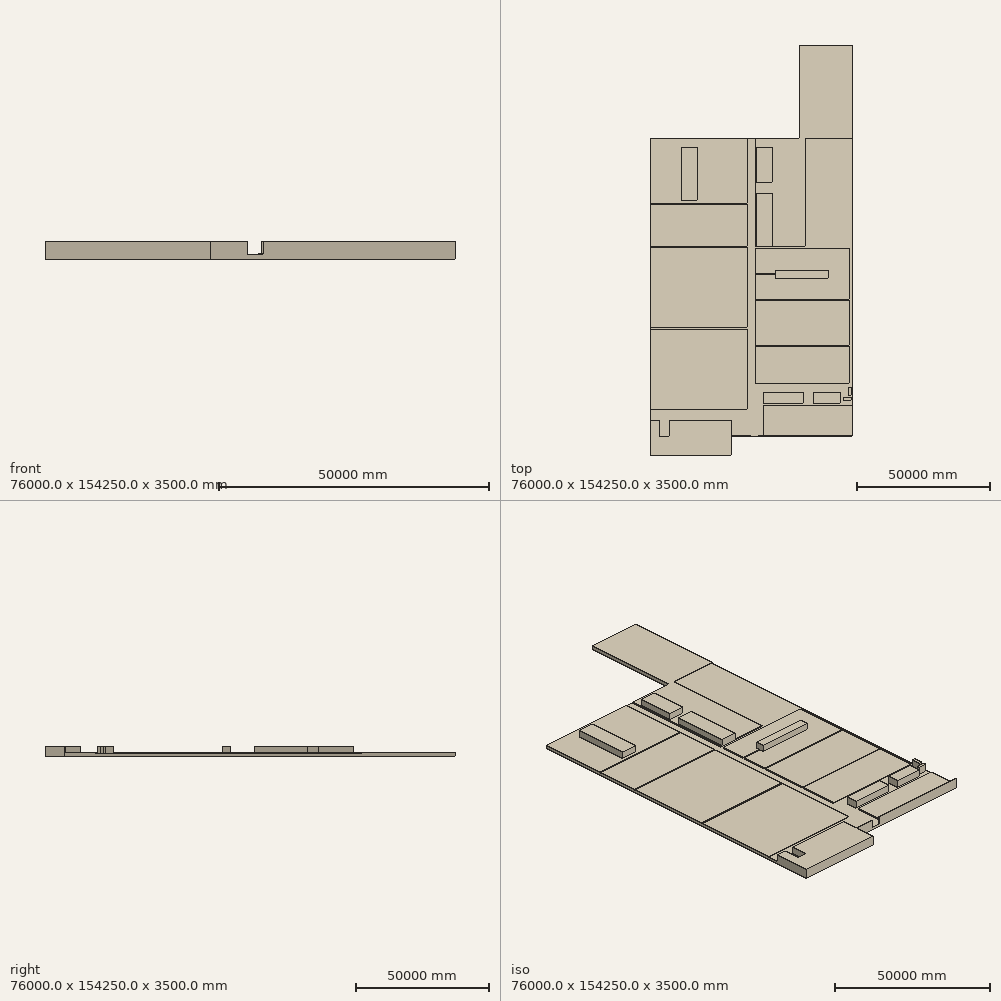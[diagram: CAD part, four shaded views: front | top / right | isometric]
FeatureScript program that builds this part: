
annotation { "Feature Type Name" : "Feature", "Feature Type Description" : "" }
export const myFeature = defineFeature(function(context is Context, id is Id, definition is map)
    precondition{}
    {
        {
            var Q0;
            Q0=qCreatedBy(makeId("Top.planeOp"),FACE);
            var sketch = newSketch(context, id + "F0", { "sketchPlane" : qUnion([Q0])});
            skLineSegment(sketch, "E0.top", {"start": v(0, 112000) * mm, "end": v(56000, 112000) * mm});
            skLineSegment(sketch, "E0.left", {"start": v(0, 0) * mm, "end": v(0, 112000) * mm});
            skLineSegment(sketch, "E0.right", {"start": v(76000, 0) * mm, "end": v(76000, 112000) * mm});
            skLineSegment(sketch, "E1", {"start": v(76000, 112000) * mm, "end": v(76000, 147000) * mm});
            skLineSegment(sketch, "E2", {"start": v(76000, 147000) * mm, "end": v(56000, 147000) * mm});
            skLineSegment(sketch, "E3", {"start": v(56000, 147000) * mm, "end": v(56000, 112000) * mm});
            skLineSegment(sketch, "E4", {"start": v(0, 0) * mm, "end": v(0, -7250) * mm});
            skLineSegment(sketch, "E5", {"start": v(0, -7250) * mm, "end": v(30500, -7250) * mm});
            skLineSegment(sketch, "E6", {"start": v(30500, -7250) * mm, "end": v(30500, -250) * mm});
            skLineSegment(sketch, "E7", {"start": v(30500, 0) * mm, "end": v(76000, 0) * mm});
            skLineSegment(sketch, "E8", {"start": v(30500, -250) * mm, "end": v(30500, -7250) * mm});
            skLineSegment(sketch, "E9", {"start": v(30500, 0) * mm, "end": v(30500, -250) * mm});
            skSolve(sketch);
        }
        {
            var Q0;
            Q0=qSketchRegion(id+"F0",true);
            extrude(context, id + "F1", {"entities" : qUnion([Q0]), "oppositeDirection" : true, "depth" : 1000 * mm});
        }
        {
            var Q0;
            Q0=makeQuery(id+"F0.imprint","IMPRINT",FACE,{"disambiguationData":[TD([[makeQuery(id+"F0.imprint","IMPRINT",EDGE,{"derivedFrom":sQuery(id+"F0.wireOp",EDGE,"E0.top")}),-1.0]])]});
            var sketch = newSketch(context, id + "F2", { "sketchPlane" : qUnion([Q0])});
            skLineSegment(sketch, "E10.bottom", {"start": v(0, 112000) * mm, "end": v(36500, 112000) * mm});
            skLineSegment(sketch, "E10.top", {"start": v(0, 87500) * mm, "end": v(36500, 87500) * mm});
            skLineSegment(sketch, "E10.left", {"start": v(0, 112000) * mm, "end": v(0, 87500) * mm});
            skLineSegment(sketch, "E10.right", {"start": v(36500, 112000) * mm, "end": v(36500, 87500) * mm});
            skLineSegment(sketch, "E11.bottom", {"start": v(0, 87000) * mm, "end": v(36500, 87000) * mm});
            skLineSegment(sketch, "E11.top", {"start": v(0, 71500) * mm, "end": v(36500, 71500) * mm});
            skLineSegment(sketch, "E11.left", {"start": v(0, 87000) * mm, "end": v(0, 71500) * mm});
            skLineSegment(sketch, "E11.right", {"start": v(36500, 87000) * mm, "end": v(36500, 71500) * mm});
            skLineSegment(sketch, "E12.bottom", {"start": v(0, 71000) * mm, "end": v(36500, 71000) * mm});
            skLineSegment(sketch, "E12.left", {"start": v(0, 71000) * mm, "end": v(0, 40750) * mm});
            skLineSegment(sketch, "E12.right", {"start": v(36500, 71000) * mm, "end": v(36500, 40750) * mm});
            skLineSegment(sketch, "E13.bottom", {"start": v(39500, 71500) * mm, "end": v(58500, 71500) * mm});
            skLineSegment(sketch, "E13.top", {"start": v(39500, 112000) * mm, "end": v(58500, 112000) * mm});
            skLineSegment(sketch, "E13.left", {"start": v(39500, 71500) * mm, "end": v(39500, 112000) * mm});
            skLineSegment(sketch, "E13.right", {"start": v(58500, 71500) * mm, "end": v(58500, 112000) * mm});
            skLineSegment(sketch, "E14.bottom", {"start": v(56000, 147000) * mm, "end": v(76000, 147000) * mm});
            skLineSegment(sketch, "E14.top", {"start": v(56000, 112000) * mm, "end": v(76000, 112000) * mm});
            skLineSegment(sketch, "E14.left", {"start": v(56000, 147000) * mm, "end": v(56000, 112000) * mm});
            skLineSegment(sketch, "E14.right", {"start": v(76000, 147000) * mm, "end": v(76000, 112000) * mm});
            skLineSegment(sketch, "E15.bottom", {"start": v(42500, 11500) * mm, "end": v(76000, 11500) * mm});
            skLineSegment(sketch, "E15.top", {"start": v(42500, 0) * mm, "end": v(76000, 0) * mm});
            skLineSegment(sketch, "E15.left", {"start": v(42500, 11500) * mm, "end": v(42500, 0) * mm});
            skLineSegment(sketch, "E15.right", {"start": v(76000, 11500) * mm, "end": v(76000, 0) * mm});
            skLineSegment(sketch, "E16.top", {"start": v(0, 10000) * mm, "end": v(36500, 10000) * mm});
            skLineSegment(sketch, "E17.bottom", {"start": v(39500, 70500) * mm, "end": v(75000, 70500) * mm});
            skLineSegment(sketch, "E17.top", {"start": v(39500, 51500) * mm, "end": v(75000, 51500) * mm});
            skLineSegment(sketch, "E17.left", {"start": v(39500, 70500) * mm, "end": v(39500, 61250) * mm});
            skLineSegment(sketch, "E17.right", {"start": v(75000, 70500) * mm, "end": v(75000, 51500) * mm});
            skLineSegment(sketch, "E18.bottom", {"start": v(39500, 51000) * mm, "end": v(75000, 51000) * mm});
            skLineSegment(sketch, "E18.top", {"start": v(39500, 34000) * mm, "end": v(75000, 34000) * mm});
            skLineSegment(sketch, "E18.left", {"start": v(39500, 51000) * mm, "end": v(39500, 34000) * mm});
            skLineSegment(sketch, "E18.right", {"start": v(75000, 51000) * mm, "end": v(75000, 34000) * mm});
            skLineSegment(sketch, "E19.bottom", {"start": v(39500, 33750) * mm, "end": v(75000, 33750) * mm});
            skLineSegment(sketch, "E19.top", {"start": v(39500, 19750) * mm, "end": v(75000, 19750) * mm});
            skLineSegment(sketch, "E19.left", {"start": v(39500, 33750) * mm, "end": v(39500, 19750) * mm});
            skLineSegment(sketch, "E19.right", {"start": v(75000, 33750) * mm, "end": v(75000, 19750) * mm});
            skLineSegment(sketch, "E20.bottom", {"start": v(39500, 61250) * mm, "end": v(47000, 61250) * mm});
            skLineSegment(sketch, "E20.top", {"start": v(39500, 60750) * mm, "end": v(47000, 60750) * mm});
            skLineSegment(sketch, "E20.right", {"start": v(47000, 61250) * mm, "end": v(47000, 60750) * mm});
            skLineSegment(sketch, "E21.trimOffspring", {"start": v(39500, 60750) * mm, "end": v(39500, 51500) * mm});
            skLineSegment(sketch, "E22", {"start": v(0, 40750) * mm, "end": v(36500, 40750) * mm});
            skLineSegment(sketch, "E23.0", {"start": v(0, 40250) * mm, "end": v(36500, 40250) * mm});
            skLineSegment(sketch, "E24.trimOffspring", {"start": v(36500, 40250) * mm, "end": v(36500, 10000) * mm});
            skLineSegment(sketch, "E25", {"start": v(0, 10000) * mm, "end": v(0, 40250) * mm});
            skLineSegment(sketch, "E26", {"start": v(18250, 71000) * mm, "end": v(18250, 40750) * mm});
            skLineSegment(sketch, "E27.trimOffspring", {"start": v(18250, 40250) * mm, "end": v(18250, 10000) * mm});
            skSolve(sketch);
        }
        {
            var Q0;
            Q0=makeQuery(id+"F0.imprint","IMPRINT",FACE,{"disambiguationData":[TD([[makeQuery(id+"F0.imprint","IMPRINT",EDGE,{"derivedFrom":sQuery(id+"F0.wireOp",EDGE,"E0.top")}),-1.0]])]});
            var sketch = newSketch(context, id + "F3", { "sketchPlane" : qUnion([Q0])});
            skLineSegment(sketch, "E28", {"start": v(30500, 6000) * mm, "end": v(7000, 6000) * mm});
            skLineSegment(sketch, "E29", {"start": v(7000, 6000) * mm, "end": v(7000, 0) * mm});
            skLineSegment(sketch, "E30", {"start": v(3500, 0) * mm, "end": v(3500, 6000) * mm});
            skLineSegment(sketch, "E31", {"start": v(3500, 6000) * mm, "end": v(0, 6000) * mm});
            skLineSegment(sketch, "E32", {"start": v(3500, 0) * mm, "end": v(7000, 0) * mm});
            skLineSegment(sketch, "E33", {"start": v(0, 0) * mm, "end": v(0, -250) * mm});
            skLineSegment(sketch, "E34.bottom", {"start": v(42500, 12500) * mm, "end": v(57500, 12500) * mm});
            skLineSegment(sketch, "E34.top", {"start": v(42500, 16500) * mm, "end": v(57500, 16500) * mm});
            skLineSegment(sketch, "E34.left", {"start": v(42500, 12500) * mm, "end": v(42500, 16500) * mm});
            skLineSegment(sketch, "E34.right", {"start": v(57500, 12500) * mm, "end": v(57500, 16500) * mm});
            skLineSegment(sketch, "E35.bottom", {"start": v(61500, 12500) * mm, "end": v(71500, 12500) * mm});
            skLineSegment(sketch, "E35.top", {"start": v(61500, 16500) * mm, "end": v(71500, 16500) * mm});
            skLineSegment(sketch, "E35.left", {"start": v(61500, 12500) * mm, "end": v(61500, 16500) * mm});
            skLineSegment(sketch, "E35.right", {"start": v(71500, 12500) * mm, "end": v(71500, 16500) * mm});
            skLineSegment(sketch, "E36", {"start": v(30500, -7250) * mm, "end": v(0, -7250) * mm});
            skLineSegment(sketch, "E37", {"start": v(0, -7250) * mm, "end": v(0, -250) * mm});
            skLineSegment(sketch, "E38.bottom", {"start": v(47000, 62500) * mm, "end": v(67000, 62500) * mm});
            skLineSegment(sketch, "E38.top", {"start": v(47000, 59500) * mm, "end": v(67000, 59500) * mm});
            skLineSegment(sketch, "E38.left", {"start": v(47000, 62500) * mm, "end": v(47000, 59500) * mm});
            skLineSegment(sketch, "E38.right", {"start": v(67000, 62500) * mm, "end": v(67000, 59500) * mm});
            skLineSegment(sketch, "E39.bottom", {"start": v(40000, 71500) * mm, "end": v(46000, 71500) * mm});
            skLineSegment(sketch, "E39.top", {"start": v(40000, 91500) * mm, "end": v(46000, 91500) * mm});
            skLineSegment(sketch, "E39.left", {"start": v(40000, 71500) * mm, "end": v(40000, 91500) * mm});
            skLineSegment(sketch, "E39.right", {"start": v(46000, 71500) * mm, "end": v(46000, 91500) * mm});
            skLineSegment(sketch, "E40.bottom", {"start": v(40000, 95500) * mm, "end": v(46000, 95500) * mm});
            skLineSegment(sketch, "E40.left", {"start": v(40000, 95500) * mm, "end": v(40000, 108500) * mm});
            skLineSegment(sketch, "E40.right", {"start": v(46000, 95500) * mm, "end": v(46000, 108500) * mm});
            skLineSegment(sketch, "E41.bottom", {"start": v(11500, 108500) * mm, "end": v(17500, 108500) * mm});
            skLineSegment(sketch, "E41.top", {"start": v(11500, 88500) * mm, "end": v(17500, 88500) * mm});
            skLineSegment(sketch, "E41.left", {"start": v(11500, 108500) * mm, "end": v(11500, 88500) * mm});
            skLineSegment(sketch, "E41.right", {"start": v(17500, 108500) * mm, "end": v(17500, 88500) * mm});
            skLineSegment(sketch, "E42.bottom", {"start": v(72500, 14500) * mm, "end": v(75500, 14500) * mm});
            skLineSegment(sketch, "E42.top", {"start": v(72500, 13500) * mm, "end": v(75500, 13500) * mm});
            skLineSegment(sketch, "E42.left", {"start": v(72500, 14500) * mm, "end": v(72500, 13500) * mm});
            skLineSegment(sketch, "E42.right", {"start": v(75500, 14500) * mm, "end": v(75500, 13500) * mm});
            skLineSegment(sketch, "E43.bottom", {"start": v(74500, 18500) * mm, "end": v(75500, 18500) * mm});
            skLineSegment(sketch, "E43.top", {"start": v(74500, 15500) * mm, "end": v(75500, 15500) * mm});
            skLineSegment(sketch, "E43.left", {"start": v(74500, 18500) * mm, "end": v(74500, 15500) * mm});
            skLineSegment(sketch, "E43.right", {"start": v(75500, 18500) * mm, "end": v(75500, 15500) * mm});
            skLineSegment(sketch, "E44", {"start": v(0, 6000) * mm, "end": v(0, 0) * mm});
            skLineSegment(sketch, "E45", {"start": v(40000, 108500) * mm, "end": v(46000, 108500) * mm});
            skLineSegment(sketch, "E46", {"start": v(30500, 6000) * mm, "end": v(30500, -7250) * mm});
            skLineSegment(sketch, "E47.bottom", {"start": v(30500, 0) * mm, "end": v(37500, 0) * mm});
            skLineSegment(sketch, "E47.top", {"start": v(30500, 250) * mm, "end": v(37500, 250) * mm});
            skLineSegment(sketch, "E47.left", {"start": v(30500, 0) * mm, "end": v(30500, 250) * mm});
            skLineSegment(sketch, "E47.right", {"start": v(37500, 0) * mm, "end": v(37500, 250) * mm});
            skLineSegment(sketch, "E48.bottom", {"start": v(40500, 0) * mm, "end": v(76000, 0) * mm});
            skLineSegment(sketch, "E48.top", {"start": v(40500, 250) * mm, "end": v(76000, 250) * mm});
            skLineSegment(sketch, "E48.left", {"start": v(40500, 0) * mm, "end": v(40500, 250) * mm});
            skLineSegment(sketch, "E48.right", {"start": v(76000, 0) * mm, "end": v(76000, 250) * mm});
            skSolve(sketch);
        }
        {
            var Q0;
            Q0=qSketchRegion(id+"F3",true);
            extrude(context, id + "F4", {"entities" : qUnion([Q0]), "operationType" : NewBodyOperationType.ADD, "depth" : 2500 * mm});
        }
        {
            var Q0;
            Q0=qSketchRegion(id+"F2",true);
            extrude(context, id + "F5", {"entities" : qUnion([Q0]), "operationType" : NewBodyOperationType.ADD, "depth" : 250 * mm});
        }
    });
